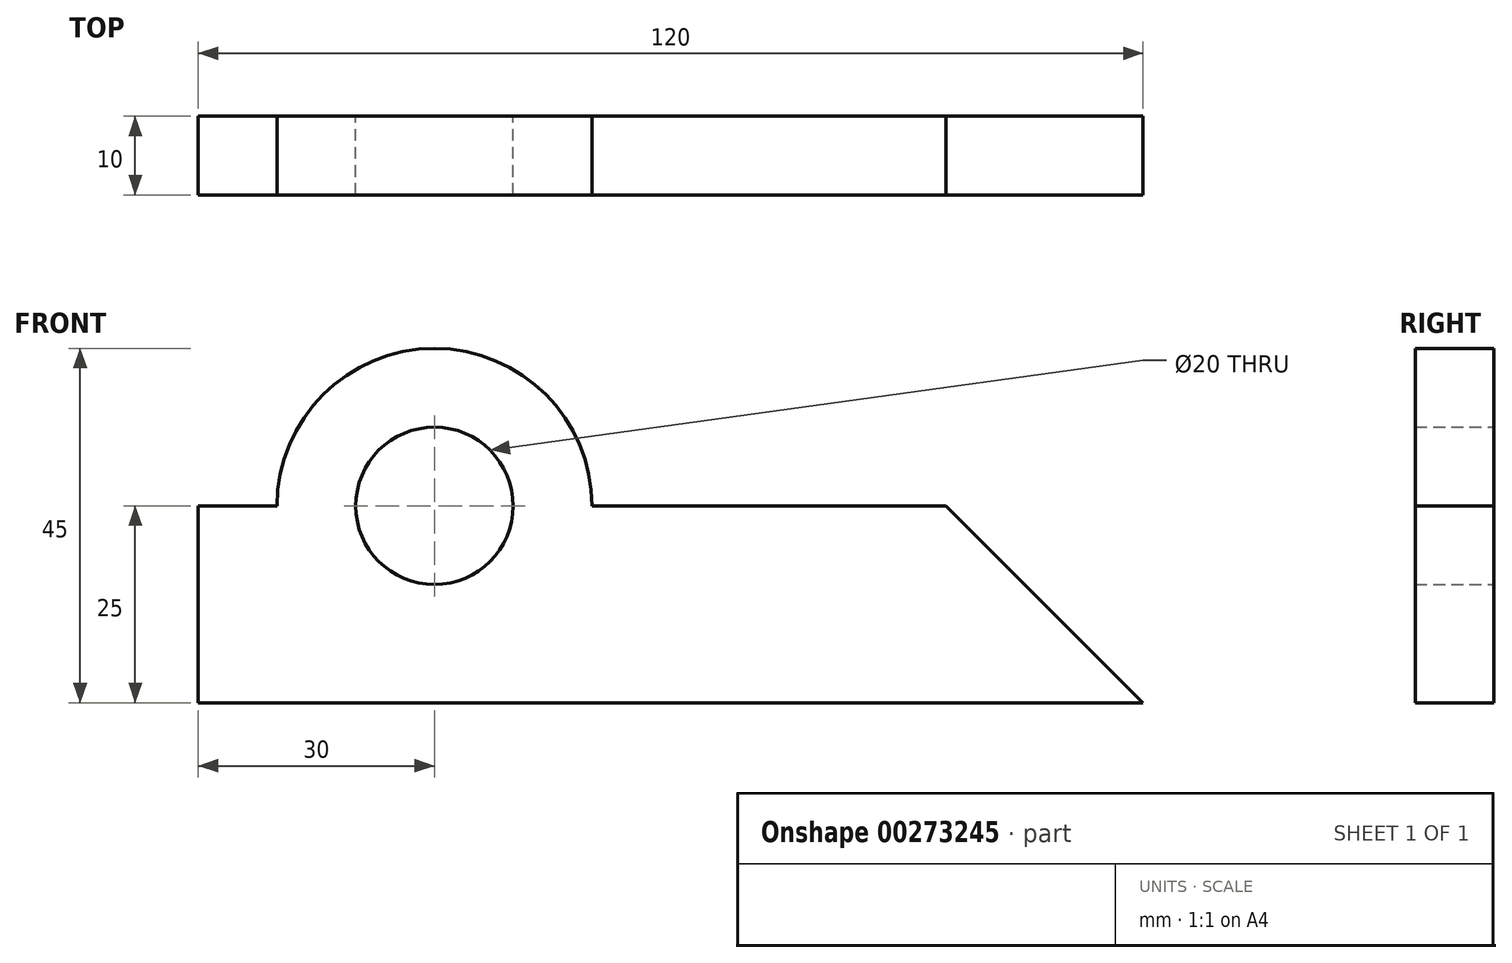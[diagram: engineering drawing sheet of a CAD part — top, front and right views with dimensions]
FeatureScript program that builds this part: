
annotation { "Feature Type Name" : "Feature", "Feature Type Description" : "" }
export const myFeature = defineFeature(function(context is Context, id is Id, definition is map)
    precondition{}
    {
        {
            var Q0;
            Q0=qCreatedBy(makeId("Front.planeOp"),FACE);
            var sketch = newSketch(context, id + "F0", { "sketchPlane" : qUnion([Q0])});
            skLineSegment(sketch, "E0", {"start": v(10, 25) * mm, "end": v(0, 25) * mm});
            skLineSegment(sketch, "E1", {"start": v(0, 25) * mm, "end": v(0, 0) * mm});
            skLineSegment(sketch, "E2", {"start": v(0, 0) * mm, "end": v(120, 0) * mm});
            skLineSegment(sketch, "E3", {"start": v(120, 0) * mm, "end": v(95, 25) * mm});
            skLineSegment(sketch, "E4", {"start": v(95, 25) * mm, "end": v(50, 25) * mm});
            skCircle(sketch, "E5", {"center": v(30, 25) * mm, "radius": 10 * mm});
            skArc(sketch, "E6", {"start": v(50, 25) * mm, "mid": v(30, 45) * mm, "end": v(10, 25) * mm});
            skSolve(sketch);
        }
        {
            var Q0;
            Q0=makeQuery(id+"F0.imprint","IMPRINT",FACE,{"disambiguationData":[TD([[makeQuery(id+"F0.imprint","IMPRINT",EDGE,{"derivedFrom":sQuery(id+"F0.wireOp",EDGE,"E0")}),1.0]])]});
            extrude(context, id + "F1", {"entities" : qUnion([Q0]), "depth" : 10 * mm});
        }
    });
